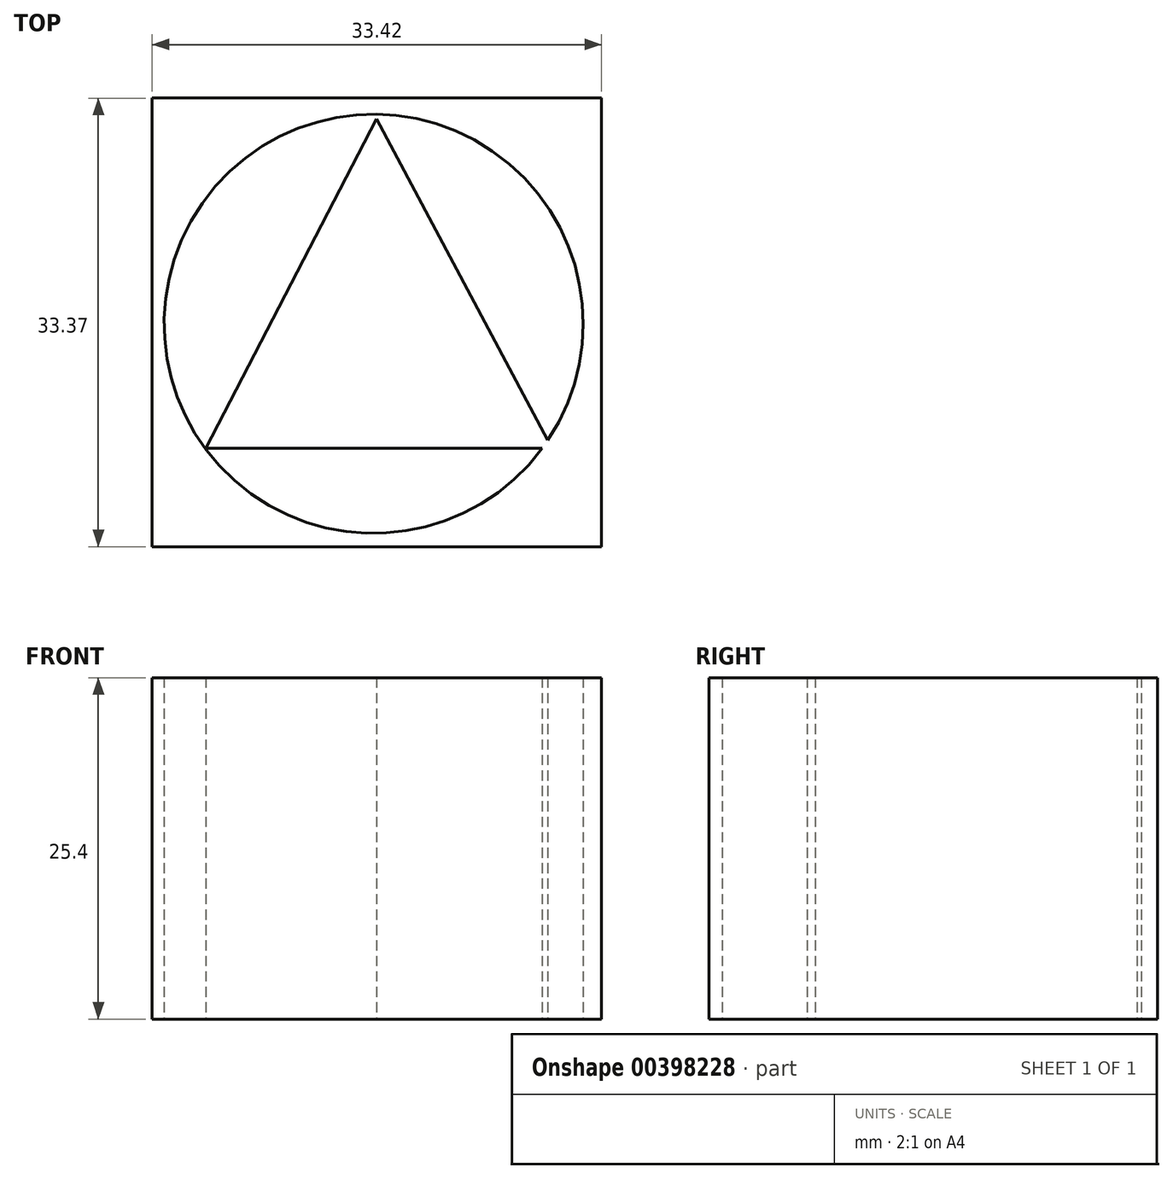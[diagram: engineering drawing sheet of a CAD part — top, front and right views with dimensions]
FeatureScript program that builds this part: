
annotation { "Feature Type Name" : "Feature", "Feature Type Description" : "" }
export const myFeature = defineFeature(function(context is Context, id is Id, definition is map)
    precondition{}
    {
        {
            var Q0;
            Q0=qCreatedBy(makeId("Top.planeOp"),FACE);
            var sketch = newSketch(context, id + "F0", { "sketchPlane" : qUnion([Q0])});
            skLineSegment(sketch, "E0.bottom", {"start": v(-17.05, 46.67) * mm, "end": v(-50.47, 46.67) * mm});
            skLineSegment(sketch, "E0.top", {"start": v(-17.05, 13.3) * mm, "end": v(-50.47, 13.3) * mm});
            skLineSegment(sketch, "E0.left", {"start": v(-17.05, 46.67) * mm, "end": v(-17.05, 13.3) * mm});
            skLineSegment(sketch, "E0.right", {"start": v(-50.47, 46.67) * mm, "end": v(-50.47, 13.3) * mm});
            skCircle(sketch, "E1", {"center": v(-34, 29.88) * mm, "radius": 15.59 * mm});
            skSolve(sketch);
        }
        {
            var Q0;
            Q0 = qSketchRegion(id + "F0", true);
            extrude(context, id + "F1", {"entities" : qUnion([Q0]), "depth" : 25.4 * mm});
        }
        {
            var Q0;
            Q0=qCreatedBy(makeId("Top.planeOp"),FACE);
            var sketch = newSketch(context, id + "F2", { "sketchPlane" : qUnion([Q0])});
            skLineSegment(sketch, "E2", {"start": v(-33.77, 45.13) * mm, "end": v(-46.49, 20.62) * mm});
            skLineSegment(sketch, "E3", {"start": v(-46.49, 20.62) * mm, "end": v(-20.73, 20.62) * mm});
            skLineSegment(sketch, "E4", {"start": v(-20.73, 20.62) * mm, "end": v(-33.77, 45.13) * mm});
            skSolve(sketch);
        }
        {
            var Q0;
            Q0 = qSketchRegion(id + "F2", true);
            extrude(context, id + "F3", {"entities" : qUnion([Q0]), "operationType" : NewBodyOperationType.ADD, "depth" : 25.4 * mm});
        }
    });
